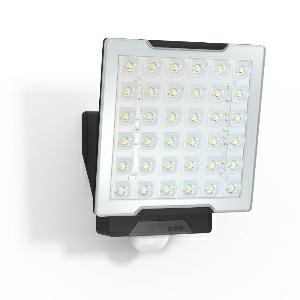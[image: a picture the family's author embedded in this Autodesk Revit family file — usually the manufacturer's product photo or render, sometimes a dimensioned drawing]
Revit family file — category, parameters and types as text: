
# Revit family: xled_pro_square_009977
name_source: partatom
category: Leuchten
revit_build: Autodesk Revit 2016 (Build: 20190508_0715(x64)
units: mm (PartAtom-declared; Revit-internal decimal feet)

## family parameters
Basisbauteil = Fläche
Beim Laden mit Abzugskörper schneiden = Nein
Bemaßung runder Anschluss = Durchmesser verwenden
Gemeinsam genutzt = Nein
Lichtquelle = Nein
Raumberechnungspunkt = Nein
Teiletyp = Normal

## types (1)
- XLED PRO Square (1 x , 2400 lm, 4000 K)
    Beschreibung = Dimensions (L x W x H): 130 x 178 x 230 mm; Mains power supply: 220 – 240 V / 50 – 60 Hz; Mounting height max.: 6,00 m; Sensor Technology: passive infrared; Output: 24,8 W; Interconnection: Yes; Type of interconnection: Sensor/slave; Interconnection, number: maximum of 10 floodlights; Luminous flux: 2400 lm; Colour temperature: 4000 K; Colour variation LED: SDCM3; Colour Rendering Index CRI: 80-89; With lamp: Yes, STEINEL LED system; Lamp: LED cannot be replaced; LED life expectancy (max. °C): 50000 h; Drop in luminous flux in accordance with LM80: L70B10; LED cooling system: Passive Thermo Control; With motion detector: Yes; Detection angle: 240 °; Angle of aperture: 180 °; Sneak-by guard: Yes; Capability of masking out individual segments: Yes; Reach, radial: r = 3 m (19 m²); Reach, tangential: r = 12 m (302 m²); Photo-cell controller: Yes; Twilight setting: 2 – 1000 lx; Time setting: 5 sec – 15 min; Basic light level function: Yes; Basic light level function time: 10 min, 30 min, all night; Soft light start: No; Continuous light: selectable, 4h; Impact resistance: IK03; IP-rating: IP54; Protection class: I; Ambient temperature: -20 – 40 °C; Housing material: Aluminium; Cover material: Plastic, transparent; Manufacturer's Warranty: 5 years; PU1, net weight: 1,818 kg; Version: black; PU1, EAN: 4007841009977
    CIE Flux Codes = 52 86 98 99 100
    Color Rendering = 80-89
    Color Temperature = 4000 K
    Frequency = 50 Hz, 60 Hz
    Height = 230 mm
    Hersteller = Steinel
    Lamp Light Flux = 2400 lm
    Lamp count = 1
    Lampe = 1 x
    Length = 130 mm
    Luminous efficacy = 100 lm/W
    ModVariant = Nein
    Modell = 009977
    Mounting Type = Surface mounted
    Number of Poles = 1
    OnlyDefault = Ja
    Power Factor = 1
    Product Name = XLED PRO Square
    Product group = Sensor-switched indoor light
    ProductGroupID = 30
    Protection Class = Protection class I
    Protection Degree = IP 54
    RlxData = <blob elided: 134289 chars, md5=866babd9>
    Scheinlast = 24 VA
    Socket = socket
    Standby Power = 0 W
    System Light Flux = 2400 lm
    System Power = 24 W
    Typenbild = produkt1_009977.jpg
    Typenkommentare = Product without accessories
    URL = http://relux.com
    VarID = ---
    Voltage = 0 V
    Vorgabe-Ansicht = 1800 mm
    Weight = 0.00 kg
    Width = 178 mm

## geometry (parser evidence)
native form markers: Sweep x10
no freeform markers — native parametric forms only
